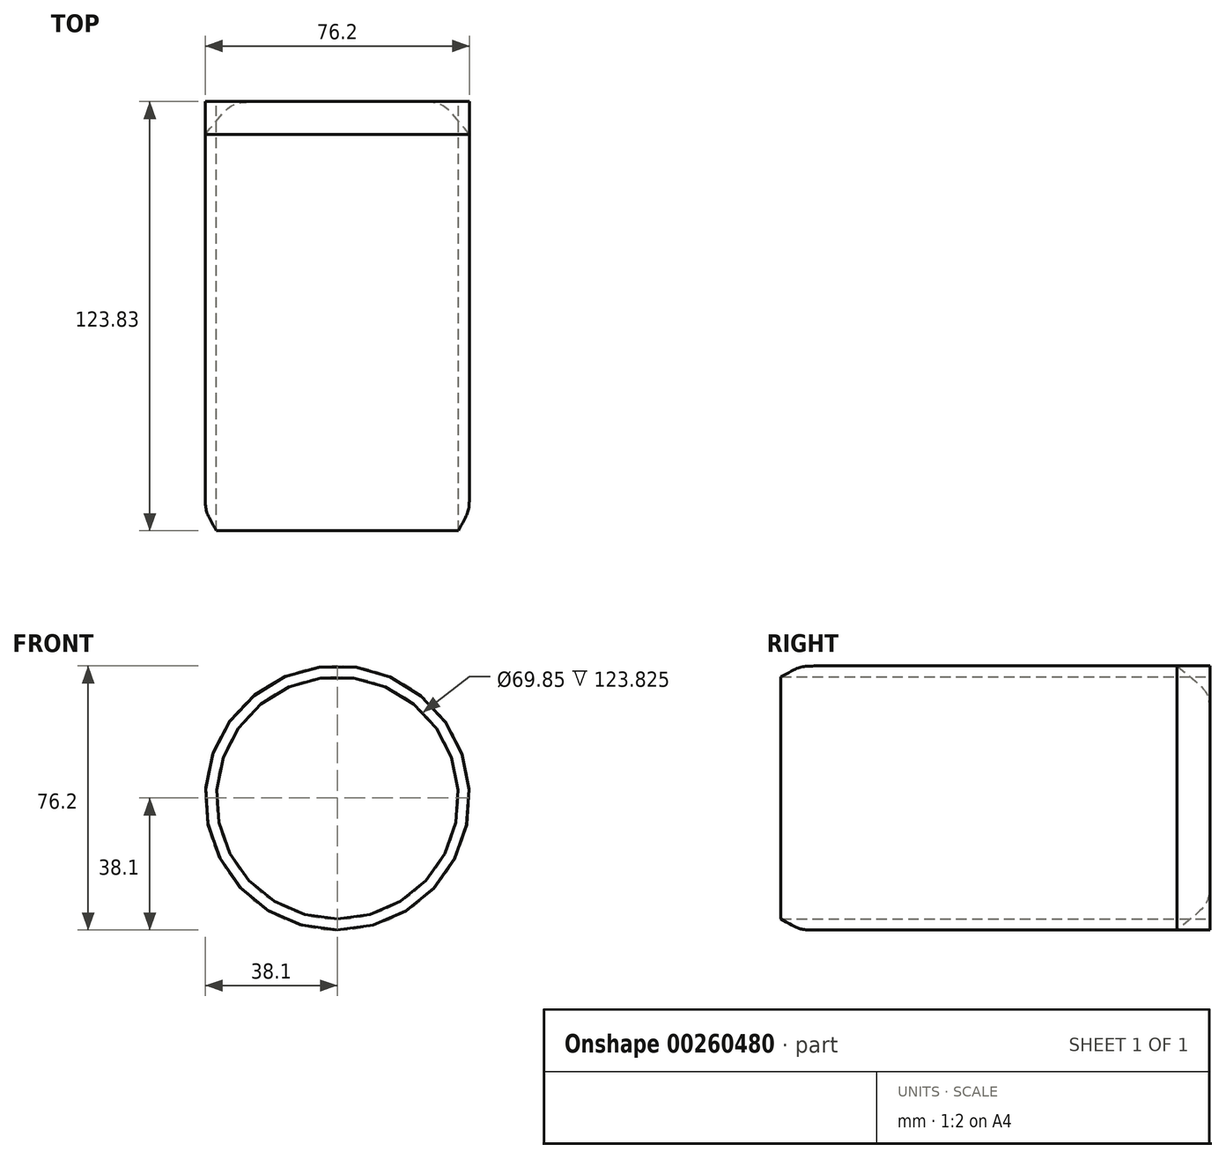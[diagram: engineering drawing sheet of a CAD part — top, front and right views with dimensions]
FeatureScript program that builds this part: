
annotation { "Feature Type Name" : "Feature", "Feature Type Description" : "" }
export const myFeature = defineFeature(function(context is Context, id is Id, definition is map)
    precondition{}
    {
        {
            var Q0;
            Q0=qCreatedBy(makeId("Front.planeOp"),FACE);
            var sketch = newSketch(context, id + "F0", { "sketchPlane" : qUnion([Q0])});
            skCircle(sketch, "E0", {"center": v(0, 0) * mm, "radius": 38.1 * mm});
            skCircle(sketch, "E1", {"center": v(0, 0) * mm, "radius": 34.93 * mm});
            skSolve(sketch);
        }
        {
            var Q0;
            Q0=makeQuery(id+"F0.imprint","IMPRINT",FACE,{"disambiguationData":[TD([[makeQuery(id+"F0.imprint","IMPRINT",EDGE,{"derivedFrom":sQuery(id+"F0.wireOp",EDGE,"E0")}),1.0]])]});
            var Q1;
            Q1=makeQuery(id+"F0.imprint","IMPRINT",FACE,{"disambiguationData":[TD([[makeQuery(id+"F0.imprint","IMPRINT",EDGE,{"derivedFrom":sQuery(id+"F0.wireOp",EDGE,"E1")}),1.0]])]});
            extrude(context, id + "F1", {"entities" : qUnion([Q0, Q1]), "depth" : 9.52 * mm});
        }
        {
            var Q0;
            Q0 = qSketchRegion(id + "F0", true);
            extrude(context, id + "F2", {"entities" : qUnion([Q0]), "depth" : 123.82 * mm});
        }
        {
            var Q0;
            Q0=makeQuery(id+"F2.opExtrude","CAP_EDGE",EDGE,{"disambiguationData":[OSD([sQuery(id+"F0.wireOp",EDGE,"E0")])],"isStart":false});
            var Q1;
            Q1=makeQuery(id+"F1.opExtrude","CAP_EDGE",EDGE,{"disambiguationData":[OSD([sQuery(id+"F0.wireOp",EDGE,"E0")])],"isStart":true});
            fillet(context, id + "F3", {"entities" : qUnion([Q0, Q1]), "radius" : 25.4 * mm, "tangentPropagation" : true, "rho" : 0.8, "crossSection" : FilletCrossSection.CONIC, "allowEdgeOverflow" : false});
        }
    });
